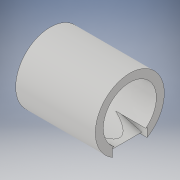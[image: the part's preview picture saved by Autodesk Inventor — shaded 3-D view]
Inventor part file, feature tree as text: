
AUTODESK INVENTOR PART (.ipt)
format: ipt  version: 2019 (Build 230136000, 136)  size: 128,000 bytes
history: native  units: in
note: dims shown in document units (in); Inventor stores cm internally (conversion verified against a paired STEP export)
features: sketch x2, plane x1, revolve x1, extrude x1
ambient origin geometry x8: Origin, YZ Plane, XZ Plane, XY Plane, X Axis, Y Axis, Z Axis, Center Point
bodies: Solid1 (feature_tree)
feature tree (5):
  plane  "Work Plane1"
  revolve  "Revolution1"  [1 undecoded]
  extrude  "Extrusion2"  TaperAngle=90.0deg  [1 undecoded]
  sketch  "Sketch2"  dims[d11=1.1811in d12=0.1181in]
  sketch  "Sketch3"  dims[d13=0.3937in d15=90.0deg d17=0.6693in d19=15.0deg d20=15.0deg d21=0.0984in d23=1.1024in d24=0.1969in d25=0.2091in d26=0.302in d27=0.5118in d28=0.0in]
note: 2 required parameter values undecoded (feature->parameter linkage not recoverable at this tier; creation-order binding heuristic only, values carry confidence <= 0.55)